# Revit family: Camera-Security-Panasonic-Dome-Network-SF138
name_source: partatom
category: Security Devices
revit_build: Autodesk Revit 2013 (Build: 20130531_2115(x64)
units: mm (PartAtom-declared; Revit-internal decimal feet)

## types (1)
- Super Dynamic FullHD, Dome, Network, WV-SF138
    Angle Of View = 100
    Audio In = Yes
    Audio Out = Yes
    Communication Ports = 10Base-T / 100Base-TX, RJ-45
    Day Or Night = Yes
    Default Elevation = 0 "
    Description = Security Camera, Super Dynamic, Full HD, Dome, Network
    Diameter = 4.094 "
    Dome Part Number = WV-CW6S
    Equipment Abbreviation = SC
    Family Version = 1.0.0
    Has POE = Yes
    Height = 1.85 "
    IP Or Analog = IP
    Indoor Or Outdoor = Indoor
    Manufacturer = Panasonic
    Minimum Illumination = 1 lx
    Model = WV-SF138
    Model Disclaimer = Contact Panasonic for more information
    Mounting Positions = Surface Mount
    Operational Humidity = 90% or less (without condensation)
    Operational Temperature = 32°F - 104°F
    Panning Range = -20 to +20
    Part Description = Security Camera, Super Dynamic, Full HD, Dome, Network
    Part Number = WV-SF138
    PoE = 48 V
    Product Documentation Link = http://cr.panasonic.com
    Product Material = ABS Resin - Panasonic - Sail White
    Product Page URL = http://security.panasonic.com
    Provide Feedback = https://www.surveymonkey.com
    Rated Current = 110 mA
    Regulatory Compliance = UL 60950-1, FCC Part 15 Class A, C-UL CAN/CSA C22.2 No.60950-1, ICES 003 Class A
    Storage Temperature = 32°F - 104°F
    Tilting Range = -20 to +90
    URL = http://security.panasonic.com
    Vandal Resistant = No
    Weight = 0.57 lb
    Wide Dynamic Range (Super Dynamic) = Yes
    z Base Radius = 2.047 "
    z Dome Material = Polycarbonate Resin - Panasonic - Smoked

## geometry (parser evidence)
native form markers: Sweep x2
no freeform markers — native parametric forms only
